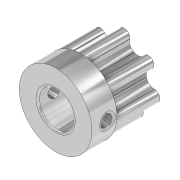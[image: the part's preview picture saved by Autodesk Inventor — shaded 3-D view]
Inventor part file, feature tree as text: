
AUTODESK INVENTOR PART (.ipt)
format: ipt  version: 2020 (Build 240168000, 168)  size: 379,904 bytes
history: native  units: in
note: dims shown in document units (in); Inventor stores cm internally (conversion verified against a paired STEP export)
features: chamfer x8, extrude x3, sketch x3, fillet x1
ambient origin geometry x8: Origin, YZ Plane, XZ Plane, XY Plane, X Axis, Y Axis, Z Axis, Center Point
bodies: Solid1 (feature_tree)
feature tree (15):
  extrude  "Extrusion1"  Depth=0.4724in
  extrude  "Extrusion2"  Depth=0.084in
  extrude  "Extrusion3"  Depth=0.084in
  chamfer  "Chamfer1"  Distance=2.7559in Angle=360.0deg
  fillet  "Fillet1"  Radius=0.2362in
  chamfer  "Chamfer3"  Distance=0.1969in
  chamfer  "Chamfer4"  Distance=0.0748in
  chamfer  "Chamfer5"  Distance=0.1575in
  chamfer  "Chamfer6"  Distance=0.2756in
  chamfer  "Chamfer7"  Distance=0.0118in
  chamfer  "Chamfer8"  Distance=0.0079in
  chamfer  "Chamfer9"  Distance=0.0394in Angle=45.0deg
  sketch  "Sketch1"  dims[d0=0.2047in d1=0.4724in]
  sketch  "Sketch2"  dims[d2=0.0866in d5=0.084in]
  sketch  "Sketch3"  dims[d6=0.084in d7=0.084in d8=2.7559in d10=360.0deg d12=0.2362in d13=0.0in d14=0.1969in d15=0.0in d16=0.0748in d17=0.1575in d18=0.0in d19=0.2756in d20=0.125in d21=0.0137in d22=0.0118in d23=0.0079in d28=0.0394in d29=0.0866in d30=45.0deg d31=0.0394in d32=0.0866in d33=45.0deg d34=0.0394in d35=0.0866in d36=45.0deg d37=0.0394in d38=0.0866in d39=45.0deg d40=0.0394in d41=0.0866in d42=45.0deg d43=0.0394in d44=0.0866in d45=45.0deg d46=0.0394in d47=0.0866in d48=45.0deg d24=0.5in d25=0.0344in d26=0.5in d27=0.0344in]
